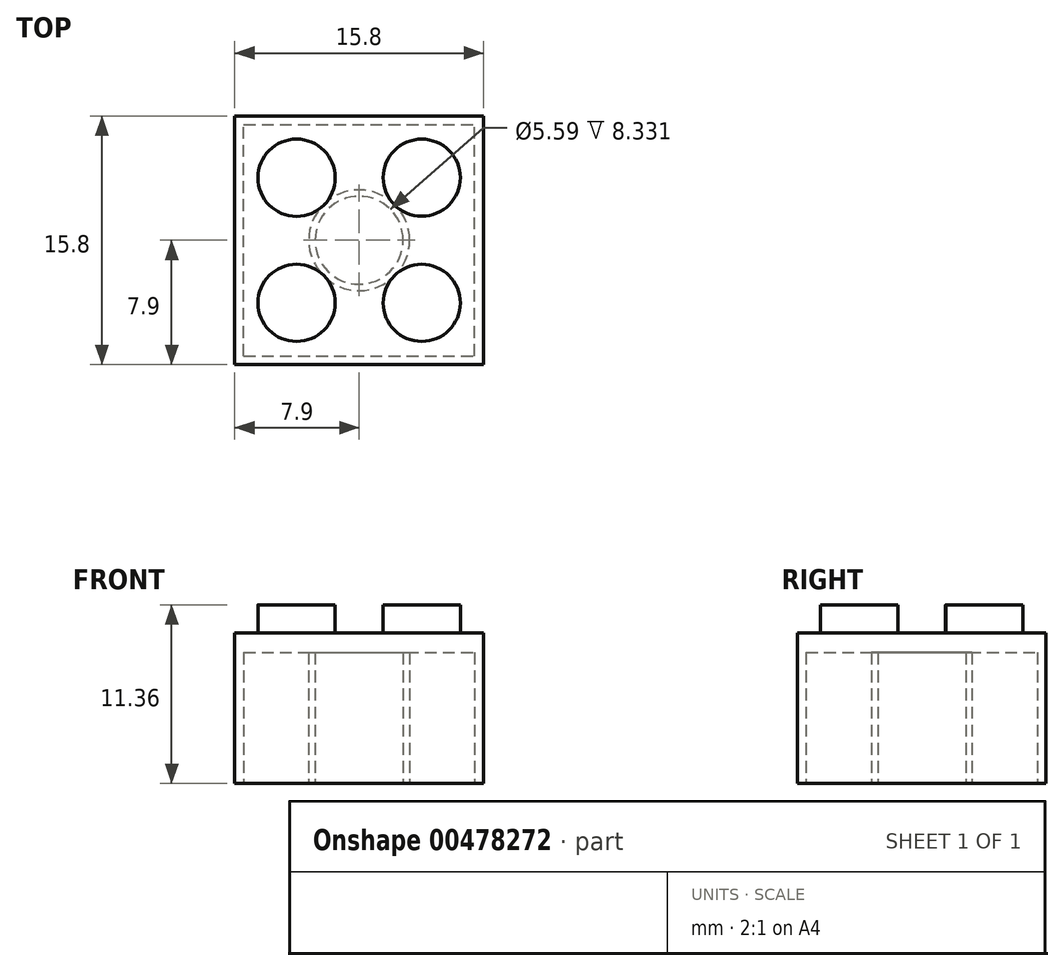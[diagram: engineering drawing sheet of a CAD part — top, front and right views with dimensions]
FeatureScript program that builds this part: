
annotation { "Feature Type Name" : "Feature", "Feature Type Description" : "" }
export const myFeature = defineFeature(function(context is Context, id is Id, definition is map)
    precondition{}
    {
        {
            var Q0;
            Q0=qCreatedBy(makeId("Top.planeOp"),FACE);
            var sketch = newSketch(context, id + "F0", { "sketchPlane" : qUnion([Q0])});
            skLineSegment(sketch, "E0.bottom", {"start": v(-7.9, 7.9) * mm, "end": v(7.9, 7.9) * mm});
            skLineSegment(sketch, "E0.top", {"start": v(-7.9, -7.9) * mm, "end": v(7.9, -7.9) * mm});
            skLineSegment(sketch, "E0.left", {"start": v(-7.9, 7.9) * mm, "end": v(-7.9, -7.9) * mm});
            skLineSegment(sketch, "E0.right", {"start": v(7.9, 7.9) * mm, "end": v(7.9, -7.9) * mm});
            skPoint(sketch, "E0.middle", {"position": v(0, 0) * mm});
            skSolve(sketch);
        }
        {
            var Q0;
            Q0=makeQuery(id+"F0.imprint","IMPRINT",FACE,{"disambiguationData":[TD([[makeQuery(id+"F0.imprint","IMPRINT",EDGE,{"derivedFrom":sQuery(id+"F0.wireOp",EDGE,"E0.bottom")}),-1.0]])]});
            extrude(context, id + "F1", {"entities" : qUnion([Q0]), "endBound" : BoundingType.SYMMETRIC, "depth" : 9.58 * mm});
        }
        {
            var Q0;
            Q0=makeQuery(id+"F1.opExtrude","CAP_FACE",FACE,{"disambiguationData":[OSD([sQuery(id+"F0.wireOp",EDGE,"E0.bottom"),sQuery(id+"F0.wireOp",EDGE,"E0.top"),sQuery(id+"F0.wireOp",EDGE,"E0.left"),sQuery(id+"F0.wireOp",EDGE,"E0.right")])],"isStart":false});
            var sketch = newSketch(context, id + "F2", { "sketchPlane" : qUnion([Q0])});
            skCircle(sketch, "E1", {"center": v(-3.98, 3.97) * mm, "radius": 2.45 * mm});
            skSolve(sketch);
        }
        {
            var Q0;
            Q0=makeQuery(id+"F2.imprint","IMPRINT",FACE,{"disambiguationData":[TD([[makeQuery(id+"F2.imprint","IMPRINT",EDGE,{"derivedFrom":sQuery(id+"F2.wireOp",EDGE,"E1")}),-1.0]])]});
            var sketch = newSketch(context, id + "F3", { "sketchPlane" : qUnion([Q0])});
            skCircle(sketch, "E2", {"center": v(3.98, 3.98) * mm, "radius": 2.45 * mm});
            skSolve(sketch);
        }
        {
            var Q0;
            Q0=makeQuery(id+"F2.imprint","IMPRINT",FACE,{"disambiguationData":[TD([[makeQuery(id+"F2.imprint","IMPRINT",EDGE,{"derivedFrom":sQuery(id+"F2.wireOp",EDGE,"E1")}),-1.0]])]});
            var sketch = newSketch(context, id + "F4", { "sketchPlane" : qUnion([Q0])});
            skCircle(sketch, "E3", {"center": v(-3.98, -3.98) * mm, "radius": 2.45 * mm});
            skSolve(sketch);
        }
        {
            var Q0;
            Q0=makeQuery(id+"F2.imprint","IMPRINT",FACE,{"disambiguationData":[TD([[makeQuery(id+"F2.imprint","IMPRINT",EDGE,{"derivedFrom":sQuery(id+"F2.wireOp",EDGE,"E1")}),-1.0]])]});
            var sketch = newSketch(context, id + "F5", { "sketchPlane" : qUnion([Q0])});
            skCircle(sketch, "E4", {"center": v(3.98, -3.98) * mm, "radius": 2.45 * mm});
            skSolve(sketch);
        }
        {
            var Q0;
            Q0=makeQuery(id+"F2.imprint","IMPRINT",FACE,{"disambiguationData":[TD([[makeQuery(id+"F2.imprint","IMPRINT",EDGE,{"derivedFrom":sQuery(id+"F2.wireOp",EDGE,"E1")}),1.0]])]});
            extrude(context, id + "F6", {"entities" : qUnion([Q0]), "operationType" : NewBodyOperationType.ADD, "depth" : 1.78 * mm, "offsetDistance" : 25.4 * mm});
        }
        {
            var Q0;
            Q0=makeQuery(id+"F3.imprint","IMPRINT",FACE,{"disambiguationData":[TD([[makeQuery(id+"F3.imprint","IMPRINT",EDGE,{"derivedFrom":sQuery(id+"F3.wireOp",EDGE,"E2")}),1.0]])]});
            extrude(context, id + "F7", {"entities" : qUnion([Q0]), "operationType" : NewBodyOperationType.ADD, "depth" : 1.78 * mm, "offsetDistance" : 25.4 * mm});
        }
        {
            var Q0;
            Q0=makeQuery(id+"F4.imprint","IMPRINT",FACE,{"disambiguationData":[TD([[makeQuery(id+"F4.imprint","IMPRINT",EDGE,{"derivedFrom":sQuery(id+"F4.wireOp",EDGE,"E3")}),1.0]])]});
            extrude(context, id + "F8", {"entities" : qUnion([Q0]), "operationType" : NewBodyOperationType.ADD, "depth" : 1.78 * mm, "offsetDistance" : 25.4 * mm});
        }
        {
            var Q0;
            Q0=makeQuery(id+"F5.imprint","IMPRINT",FACE,{"disambiguationData":[TD([[makeQuery(id+"F5.imprint","IMPRINT",EDGE,{"derivedFrom":sQuery(id+"F5.wireOp",EDGE,"E4")}),1.0]])]});
            extrude(context, id + "F9", {"entities" : qUnion([Q0]), "operationType" : NewBodyOperationType.ADD, "depth" : 1.78 * mm});
        }
        {
            var Q0;
            Q0=makeQuery(id+"F1.opExtrude","CAP_FACE",FACE,{"disambiguationData":[OSD([sQuery(id+"F0.wireOp",EDGE,"E0.bottom"),sQuery(id+"F0.wireOp",EDGE,"E0.top"),sQuery(id+"F0.wireOp",EDGE,"E0.left"),sQuery(id+"F0.wireOp",EDGE,"E0.right")])],"isStart":true});
            var sketch = newSketch(context, id + "F10", { "sketchPlane" : qUnion([Q0])});
            skLineSegment(sketch, "E5.bottom", {"start": v(-7.33, 7.35) * mm, "end": v(7.33, 7.35) * mm});
            skLineSegment(sketch, "E5.top", {"start": v(-7.33, -7.35) * mm, "end": v(7.33, -7.35) * mm});
            skLineSegment(sketch, "E5.left", {"start": v(-7.33, 7.35) * mm, "end": v(-7.33, -7.35) * mm});
            skLineSegment(sketch, "E5.right", {"start": v(7.33, 7.35) * mm, "end": v(7.33, -7.35) * mm});
            skPoint(sketch, "E5.middle", {"position": v(0, 0) * mm});
            skSolve(sketch);
        }
        {
            var Q0;
            Q0=makeQuery(id+"F10.imprint","IMPRINT",FACE,{"disambiguationData":[TD([[makeQuery(id+"F10.imprint","IMPRINT",EDGE,{"derivedFrom":sQuery(id+"F10.wireOp",EDGE,"E5.bottom")}),-1.0]])]});
            var sketch = newSketch(context, id + "F11", { "sketchPlane" : qUnion([Q0])});
            skCircle(sketch, "E6", {"center": v(0, 0) * mm, "radius": 3.2 * mm});
            skSolve(sketch);
        }
        {
            var Q0;
            Q0=makeQuery(id+"F10.imprint","IMPRINT",FACE,{"disambiguationData":[TD([[makeQuery(id+"F10.imprint","IMPRINT",EDGE,{"derivedFrom":sQuery(id+"F10.wireOp",EDGE,"E5.bottom")}),-1.0]])]});
            var sketch = newSketch(context, id + "F12", { "sketchPlane" : qUnion([Q0])});
            skCircle(sketch, "E7", {"center": v(0, 0) * mm, "radius": 2.8 * mm});
            skSolve(sketch);
        }
        {
            var Q0;
            Q0=makeQuery(id+"F10.imprint","IMPRINT",FACE,{"disambiguationData":[TD([[makeQuery(id+"F10.imprint","IMPRINT",EDGE,{"derivedFrom":sQuery(id+"F10.wireOp",EDGE,"E5.bottom")}),-1.0]])]});
            extrude(context, id + "F13", {"entities" : qUnion([Q0]), "operationType" : NewBodyOperationType.REMOVE, "oppositeDirection" : true, "depth" : 8.33 * mm, "offsetDistance" : 25.4 * mm});
        }
        {
            var Q0;
            Q0=makeQuery(id+"F11.imprint","IMPRINT",FACE,{"disambiguationData":[TD([[makeQuery(id+"F11.imprint","IMPRINT",EDGE,{"derivedFrom":sQuery(id+"F11.wireOp",EDGE,"E6")}),1.0]])]});
            extrude(context, id + "F14", {"entities" : qUnion([Q0]), "operationType" : NewBodyOperationType.ADD, "oppositeDirection" : true, "depth" : 8.33 * mm, "offsetDistance" : 25.4 * mm});
        }
        {
            var Q0;
            Q0 = qSketchRegion(id + "F12", true);
            extrude(context, id + "F15", {"entities" : qUnion([Q0]), "operationType" : NewBodyOperationType.REMOVE, "oppositeDirection" : true, "depth" : 8.33 * mm, "offsetDistance" : 25.4 * mm});
        }
    });
